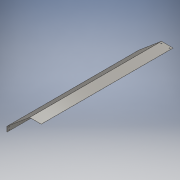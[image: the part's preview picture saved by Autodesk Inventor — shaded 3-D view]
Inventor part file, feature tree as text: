
AUTODESK INVENTOR PART (.ipt)
format: ipt  version: 2016 (Build 200138000, 138)  size: 192,000 bytes
history: native  units: mm
features: sheet_metal_op x7, sketch x5, other x4, hole x2
ambient origin geometry x8: Origin, YZ Plane, XZ Plane, XY Plane, X Axis, Y Axis, Z Axis, Center Point
bodies: Solid1 (feature_tree)
feature tree (18):
  sheet_metal_op  "Face1"
  sheet_metal_op  "Flange1"
  sheet_metal_op  "Flange2"
  hole  "Hole1"  [1 undecoded]
  hole  "Hole2"  [1 undecoded]
  sketch  "Sketch1"  dims[d0=150.0mm d1=1695.0mm]
  other  "Plate1"
  sketch  "Sketch2"  dims[d2=1.6mm d3=1.6mm]
  other  "Plate2"
  sheet_metal_op  "Bend1"
  sheet_metal_op  "Corner1"
  sketch  "Sketch3"  dims[d4=0.8mm]
  other  "Plate3"
  sheet_metal_op  "Bend2"
  sheet_metal_op  "Corner2"
  sketch  "Sketch4"  dims[d5=3.2mm]
  sketch  "Sketch5"  dims[d6=1.6mm d7=380.0mm d8=6.981317mm d9=1.6mm d10=6.4mm d11=1.6mm d12=1.6mm d13=1.6mm d14=0.8mm d15=3.2mm d16=1.6mm d17=65.0mm d18=8.726646mm d19=1.6mm d20=6.4mm d21=1.6mm d22=1.6mm d24=12.0mm d26=25.0mm d27=15.0mm d28=12.0mm d29=15.0mm d30=12.0mm d31=12.0mm d32=25.0mm d33=25.0mm d34=12.0mm d35=6.0mm d36=4.0mm d37=2.0mm d38=90.0deg d39=1.6mm d40=20.594885mm d42=12.0mm d43=25.0mm d44=20.0mm d45=12.0mm d46=20.0mm d47=12.0mm d48=6.0mm d49=4.0mm d50=2.0mm d51=90.0deg d52=1.6mm d53=20.594885mm]
  other  "Definition1"
note: 2 required parameter values undecoded (feature->parameter linkage not recoverable at this tier; creation-order binding heuristic only, values carry confidence <= 0.55)
